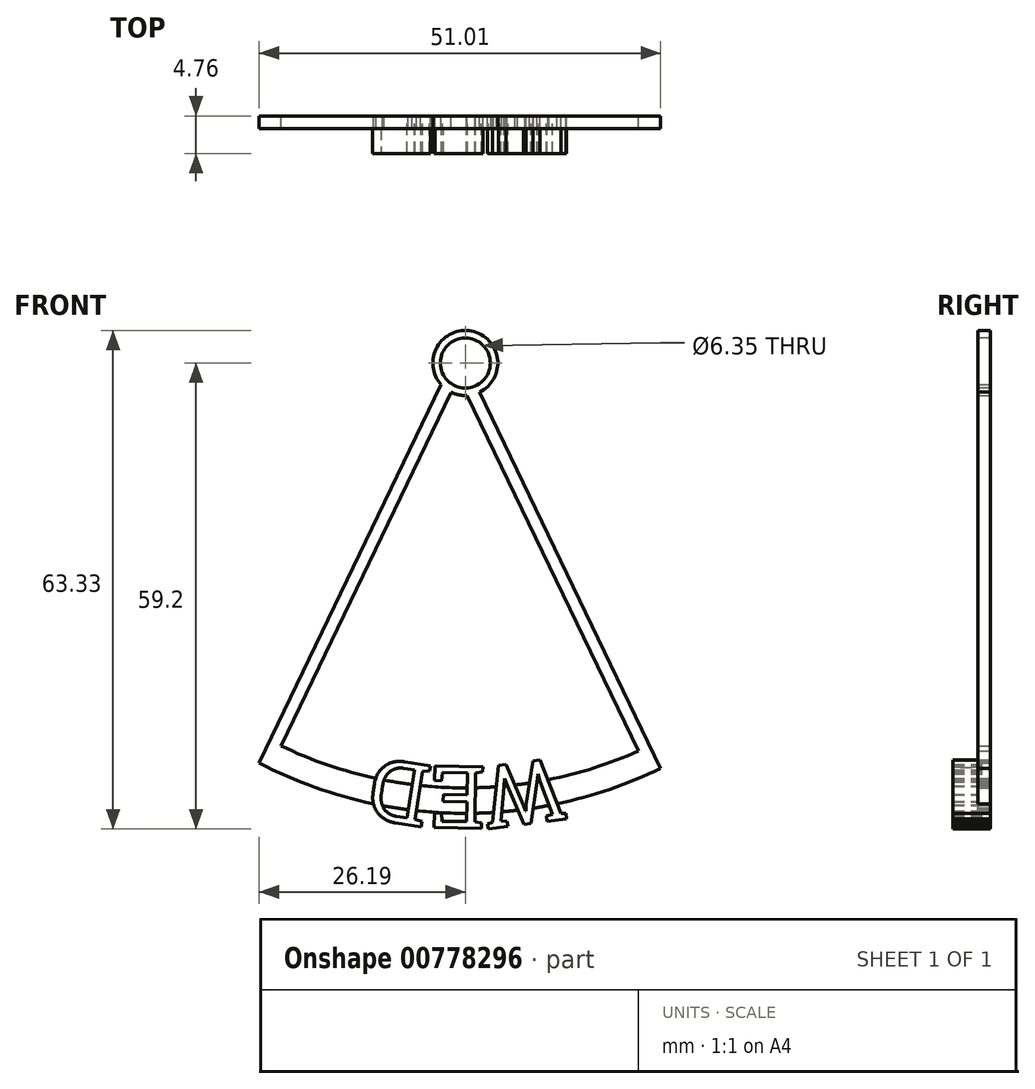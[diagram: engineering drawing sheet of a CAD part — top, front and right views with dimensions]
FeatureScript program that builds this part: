
annotation { "Feature Type Name" : "Feature", "Feature Type Description" : "" }
export const myFeature = defineFeature(function(context is Context, id is Id, definition is map)
    precondition{}
    {
        {
            var Q0;
            Q0=qCreatedBy(makeId("Front.planeOp"),FACE);
            var sketch = newSketch(context, id + "F0", { "sketchPlane" : qUnion([Q0])});
            skCircle(sketch, "E0", {"center": v(0, 0) * mm, "radius": 59.18 * mm, "construction": true});
            skCircle(sketch, "E1", {"center": v(0, 0) * mm, "radius": 50.8 * mm, "construction": true});
            skLineSegment(sketch, "E2", {"start": v(0, 0) * mm, "end": v(0, 59.18) * mm, "construction": true});
            skLineSegment(sketch, "E3", {"start": v(0, 0) * mm, "end": v(25.7, -53.3) * mm, "construction": true});
            skLineSegment(sketch, "E4", {"start": v(0, 0) * mm, "end": v(7.64, -58.69) * mm, "construction": true});
            skLineSegment(sketch, "E5", {"start": v(0, 0) * mm, "end": v(-1.12, -59.17) * mm, "construction": true});
            skLineSegment(sketch, "E6", {"start": v(0, 0) * mm, "end": v(-9.09, -58.48) * mm, "construction": true});
            skText(sketch, "E7", { "text": "W", "fontName": "RobotoSlab-Regular.ttf"});
            skText(sketch, "E8", { "text": "E", "fontName": "RobotoSlab-Regular.ttf"});
            skText(sketch, "E9", { "text": "D", "fontName": "RobotoSlab-Regular.ttf"});
            skLineSegment(sketch, "E10", {"start": v(0, 0) * mm, "end": v(13, -57.99) * mm, "construction": true});
            skLineSegment(sketch, "E11", {"start": v(0, 0) * mm, "end": v(-12.92, -57.89) * mm, "construction": true});
            skLineSegment(sketch, "E12", {"start": v(0, 0) * mm, "end": v(-25.65, -53.34) * mm, "construction": true});
            const initialGuessF0  = {"E7": [0.01198, -0.05012, -0.99163, -0.1291, 0.00794], "E8": [0.0026, -0.0513, -0.99982, 0.0189, 0.00794], "E9": [-0.00404, -0.05123, -0.98814, 0.15355, 0.00794]};
            skSetInitialGuess(sketch, initialGuessF0);
            skSolve(sketch);
        }
        {
            var Q0;
            Q0=qSketchRegion(id+"F0",true);
            extrude(context, id + "F1", {"entities" : qUnion([Q0]), "depth" : 4.76 * mm, "offsetDistance" : 25.4 * mm});
        }
        {
            var Q0;
            Q0=qCreatedBy(makeId("Front.planeOp"),FACE);
            var sketch = newSketch(context, id + "F2", { "sketchPlane" : qUnion([Q0])});
            skCircle(sketch, "E13", {"center": v(0, 0) * mm, "radius": 4.13 * mm, "construction": true});
            skCircle(sketch, "E14", {"center": v(0, 0) * mm, "radius": 53.98 * mm, "construction": true});
            skCircle(sketch, "E15", {"center": v(0, 0) * mm, "radius": 57.15 * mm, "construction": true});
            skLineSegment(sketch, "E16", {"start": v(0, 0) * mm, "end": v(0, 57.15) * mm, "construction": true});
            skLineSegment(sketch, "E17", {"start": v(0, 0) * mm, "end": v(24.82, -51.48) * mm, "construction": true});
            skLineSegment(sketch, "E18", {"start": v(0, 0) * mm, "end": v(-23.39, -48.64) * mm, "construction": true});
            skLineSegment(sketch, "E19", {"start": v(22, -49.29) * mm, "end": v(0.22, -4.12) * mm, "construction": true});
            skLineSegment(sketch, "E20", {"start": v(-26.19, -50.8) * mm, "end": v(-3.08, -2.75) * mm, "construction": true});
            skLineSegment(sketch, "E21", {"start": v(-3.08, -2.75) * mm, "end": v(-26.19, -50.8) * mm});
            skLineSegment(sketch, "E22", {"start": v(-23.39, -48.64) * mm, "end": v(-1.79, -3.72) * mm});
            skLineSegment(sketch, "E23", {"start": v(24.82, -51.48) * mm, "end": v(1.8, -3.72) * mm});
            skLineSegment(sketch, "E24", {"start": v(22, -49.29) * mm, "end": v(0.22, -4.12) * mm});
            skCircle(sketch, "E25", {"center": v(0, 0) * mm, "radius": 4.13 * mm});
            skArc(sketch, "E26", {"start": v(-23.39, -48.64) * mm, "mid": v(-0.77, -53.97) * mm, "end": v(22, -49.29) * mm});
            skArc(sketch, "E27", {"start": v(-26.19, -50.8) * mm, "mid": v(-0.76, -57.2) * mm, "end": v(24.82, -51.48) * mm});
            skSolve(sketch);
        }
        {
            var Q0;
            {var subQ0=sQuery(id+"F2.wireOp",EDGE,"E25");var subQ1=makeQuery(id+"F2.imprint","INTERSECT",VERTEX,{"derivedFrom":[sQuery(id+"F2.wireOp",EDGE,"E21"),subQ0]});Q0=makeQuery(id+"F2.imprint","IMPRINT",FACE,{"disambiguationData":[TD([[makeQuery(id+"F2.imprint","IMPRINT",EDGE,{"disambiguationData":[TD([[subQ1,-1.0]])],"derivedFrom":subQ0}),1.0]])]});}
            var Q1;
            {var subQ3=sQuery(id+"F2.wireOp",EDGE,"E21");Q1=makeQuery(id+"F2.imprint","IMPRINT",FACE,{"disambiguationData":[TD([[makeQuery(id+"F2.imprint","IMPRINT",EDGE,{"derivedFrom":subQ3}),1.0]])]});}
            extrude(context, id + "F3", {"entities" : qUnion([Q0, Q1]), "operationType" : NewBodyOperationType.ADD, "depth" : 1.59 * mm, "offsetDistance" : 25.4 * mm});
        }
        {
            var Q0;
            {var subQ0=sQuery(id+"F2.wireOp",EDGE,"E25");var subQ1=sQuery(id+"F2.wireOp",EDGE,"E21");var subQ2=sQuery(id+"F2.wireOp",EDGE,"E23");var subQ3=sQuery(id+"F2.wireOp",EDGE,"E22");var subQ4=sQuery(id+"F2.wireOp",EDGE,"E24");var subQ5=sQuery(id+"F2.wireOp",EDGE,"E26");var subQ6=sQuery(id+"F2.wireOp",EDGE,"E27");Q0=makeQuery(id+"F3.boolean.opBoolean","SPLIT",FACE,{"disambiguationData":[TD([makeQuery(id+"F1.opExtrude","SWEPT_FACE",FACE,{"disambiguationData":[OSD([sQuery(id+"F0.wireOp",EDGE,"E7.sketch_text.stroke-25")])]})])],"derivedFrom":makeQuery(id+"F3.opExtrude","CAP_FACE",FACE,{"disambiguationData":[OSD([subQ1,subQ3,subQ2,subQ4,subQ0,subQ5,subQ6])],"isStart":false})});}
            var sketch = newSketch(context, id + "F4", { "sketchPlane" : qUnion([Q0])});
            skPoint(sketch, "E28", {"position": v(0, 0) * mm});
            skSolve(sketch);
        }
        {
            var Q0;
            Q0=sQuery(id+"F4.wireOp",VERTEX,"E28");
            var Q1;
            Q1=makeQuery(id+"F1.opExtrude","SWEPT_BODY",BODY,{"disambiguationData":[OSD([sQuery(id+"F0.wireOp",EDGE,"E7.sketch_text.stroke-0"),sQuery(id+"F0.wireOp",EDGE,"E7.sketch_text.stroke-1"),sQuery(id+"F0.wireOp",EDGE,"E7.sketch_text.stroke-2"),sQuery(id+"F0.wireOp",EDGE,"E7.sketch_text.stroke-3"),sQuery(id+"F0.wireOp",EDGE,"E7.sketch_text.stroke-4"),sQuery(id+"F0.wireOp",EDGE,"E7.sketch_text.stroke-5"),sQuery(id+"F0.wireOp",EDGE,"E7.sketch_text.stroke-6"),sQuery(id+"F0.wireOp",EDGE,"E7.sketch_text.stroke-7"),sQuery(id+"F0.wireOp",EDGE,"E7.sketch_text.stroke-8"),sQuery(id+"F0.wireOp",EDGE,"E7.sketch_text.stroke-9"),sQuery(id+"F0.wireOp",EDGE,"E7.sketch_text.stroke-10"),sQuery(id+"F0.wireOp",EDGE,"E7.sketch_text.stroke-11"),sQuery(id+"F0.wireOp",EDGE,"E7.sketch_text.stroke-12"),sQuery(id+"F0.wireOp",EDGE,"E7.sketch_text.stroke-13"),sQuery(id+"F0.wireOp",EDGE,"E7.sketch_text.stroke-14"),sQuery(id+"F0.wireOp",EDGE,"E7.sketch_text.stroke-15"),sQuery(id+"F0.wireOp",EDGE,"E7.sketch_text.stroke-16"),sQuery(id+"F0.wireOp",EDGE,"E7.sketch_text.stroke-17"),sQuery(id+"F0.wireOp",EDGE,"E7.sketch_text.stroke-18"),sQuery(id+"F0.wireOp",EDGE,"E7.sketch_text.stroke-19"),sQuery(id+"F0.wireOp",EDGE,"E7.sketch_text.stroke-20"),sQuery(id+"F0.wireOp",EDGE,"E7.sketch_text.stroke-21"),sQuery(id+"F0.wireOp",EDGE,"E7.sketch_text.stroke-22"),sQuery(id+"F0.wireOp",EDGE,"E7.sketch_text.stroke-23"),sQuery(id+"F0.wireOp",EDGE,"E7.sketch_text.stroke-24"),sQuery(id+"F0.wireOp",EDGE,"E7.sketch_text.stroke-25"),sQuery(id+"F0.wireOp",EDGE,"E7.sketch_text.stroke-26"),sQuery(id+"F0.wireOp",EDGE,"E7.sketch_text.stroke-27"),sQuery(id+"F0.wireOp",EDGE,"E7.sketch_text.stroke-28"),sQuery(id+"F0.wireOp",EDGE,"E7.sketch_text.stroke-29")])]});
            hole(context, id + "F5", {"style" : HoleStyle.SIMPLE, "endStyle" : HoleEndStyle.THROUGH, "holeDiameter" : 6.35 * mm, "majorDiameter" : 6.35 * mm, "isTappedThrough" : true, "tappedDepth" : 12.7 * mm, "tapClearance" : 3, "locations" : qUnion([Q0]), "scope" : qUnion([Q1])});
        }
    });
